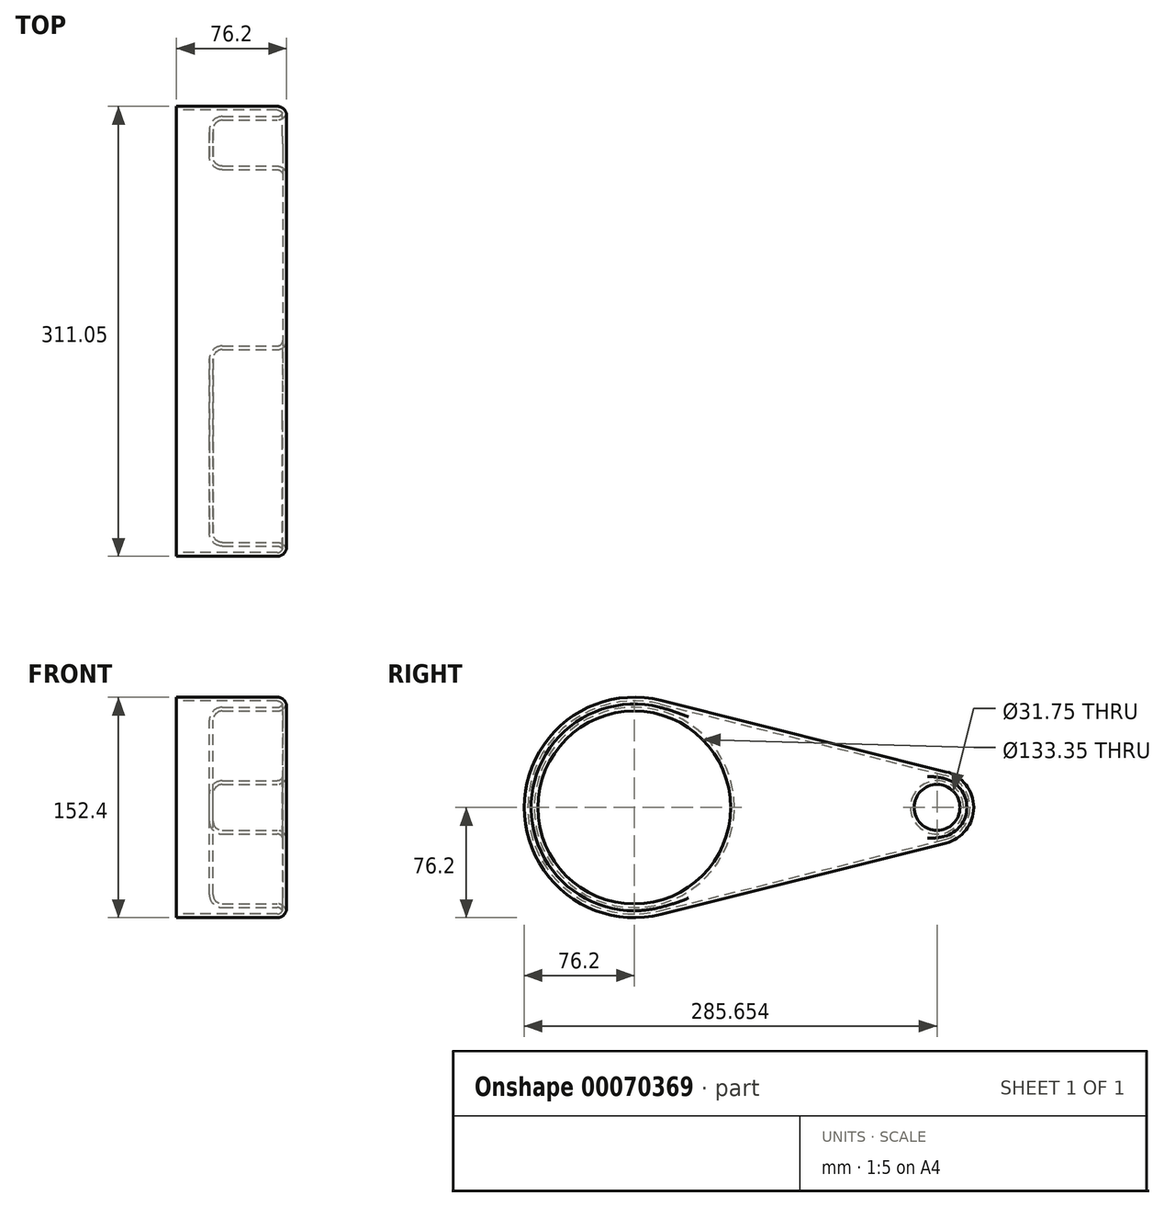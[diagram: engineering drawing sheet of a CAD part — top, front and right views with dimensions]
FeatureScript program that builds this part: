
annotation { "Feature Type Name" : "Feature", "Feature Type Description" : "" }
export const myFeature = defineFeature(function(context is Context, id is Id, definition is map)
    precondition{}
    {
        {
            var Q0;
            Q0=qCreatedBy(makeId("Right.planeOp"),FACE);
            var sketch = newSketch(context, id + "F0", { "sketchPlane" : qUnion([Q0])});
            skCircle(sketch, "E0", {"center": v(0, 0) * mm, "radius": 76.2 * mm});
            skCircle(sketch, "E1", {"center": v(209.45, 0) * mm, "radius": 25.4 * mm});
            skLineSegment(sketch, "E2", {"start": v(18.48, 73.92) * mm, "end": v(215.61, 24.64) * mm});
            skLineSegment(sketch, "E3", {"start": v(18.48, -73.92) * mm, "end": v(215.61, -24.64) * mm});
            skSolve(sketch);
        }
        {
            var Q0;
            {var subQ0=sQuery(id+"F0.wireOp",EDGE,"E0");var subQ1=makeQuery(id+"F0.imprint","INTERSECT",VERTEX,{"derivedFrom":[subQ0,sQuery(id+"F0.wireOp",EDGE,"E2")]});Q0=makeQuery(id+"F0.imprint","IMPRINT",FACE,{"disambiguationData":[TD([[makeQuery(id+"F0.imprint","IMPRINT",EDGE,{"disambiguationData":[TD([[subQ1,-1.0]])],"derivedFrom":subQ0}),1.0]])]});}
            var Q1;
            {var subQ0=sQuery(id+"F0.wireOp",EDGE,"E2");Q1=makeQuery(id+"F0.imprint","IMPRINT",FACE,{"disambiguationData":[TD([[makeQuery(id+"F0.imprint","IMPRINT",EDGE,{"derivedFrom":subQ0}),-1.0]])]});}
            var Q2;
            {var subQ0=sQuery(id+"F0.wireOp",EDGE,"E1");var subQ1=makeQuery(id+"F0.imprint","INTERSECT",VERTEX,{"derivedFrom":[subQ0,sQuery(id+"F0.wireOp",EDGE,"E2")]});Q2=makeQuery(id+"F0.imprint","IMPRINT",FACE,{"disambiguationData":[TD([[makeQuery(id+"F0.imprint","IMPRINT",EDGE,{"disambiguationData":[TD([[subQ1,-1.0]])],"derivedFrom":subQ0}),1.0]])]});}
            extrude(context, id + "F1", {"entities" : qUnion([Q0, Q1, Q2]), "depth" : 76.2 * mm});
        }
        {
            var Q0;
            Q0=makeQuery(id+"F1.opExtrude","CAP_FACE",FACE,{"disambiguationData":[OSD([sQuery(id+"F0.wireOp",EDGE,"E0"),sQuery(id+"F0.wireOp",EDGE,"E1"),sQuery(id+"F0.wireOp",EDGE,"E2"),sQuery(id+"F0.wireOp",EDGE,"E3")])],"isStart":false});
            var sketch = newSketch(context, id + "F2", { "sketchPlane" : qUnion([Q0])});
            skCircle(sketch, "E4", {"center": v(0, 0) * mm, "radius": 66.68 * mm});
            skCircle(sketch, "E5", {"center": v(209.45, 0) * mm, "radius": 15.88 * mm});
            skSolve(sketch);
        }
        {
            var Q0;
            Q0=makeQuery(id+"F2.imprint","IMPRINT",FACE,{"disambiguationData":[TD([[makeQuery(id+"F2.imprint","IMPRINT",EDGE,{"derivedFrom":sQuery(id+"F2.wireOp",EDGE,"E4")}),1.0]])]});
            var Q1;
            Q1=makeQuery(id+"F2.imprint","IMPRINT",FACE,{"disambiguationData":[TD([[makeQuery(id+"F2.imprint","IMPRINT",EDGE,{"derivedFrom":sQuery(id+"F2.wireOp",EDGE,"E5")}),1.0]])]});
            extrude(context, id + "F3", {"entities" : qUnion([Q0, Q1]), "operationType" : NewBodyOperationType.REMOVE, "oppositeDirection" : true, "depth" : 50.8 * mm});
        }
        {
            var Q0;
            Q0=makeQuery(id+"F1.opExtrude","CAP_FACE",FACE,{"disambiguationData":[OSD([sQuery(id+"F0.wireOp",EDGE,"E0"),sQuery(id+"F0.wireOp",EDGE,"E1"),sQuery(id+"F0.wireOp",EDGE,"E2"),sQuery(id+"F0.wireOp",EDGE,"E3")])],"isStart":false});
            var Q1;
            Q1=makeQuery(id+"F3.boolean.opBoolean","COPY",FACE,{"derivedFrom":makeQuery(id+"F3.opExtrude","CAP_FACE",FACE,{"disambiguationData":[OSD([sQuery(id+"F2.wireOp",EDGE,"E4")])],"isStart":false})});
            var Q2;
            Q2=makeQuery(id+"F3.boolean.opBoolean","COPY",EDGE,{"derivedFrom":makeQuery(id+"F3.opExtrude","CAP_EDGE",EDGE,{"disambiguationData":[OSD([sQuery(id+"F2.wireOp",EDGE,"E5")])],"isStart":false})});
            fillet(context, id + "F4", {"entities" : qUnion([Q0, Q1, Q2]), "radius" : 6.35 * mm, "tangentPropagation" : true, "allowEdgeOverflow" : false});
        }
        {
            var Q0;
            Q0=makeQuery(id+"F1.opExtrude","CAP_FACE",FACE,{"disambiguationData":[OSD([sQuery(id+"F0.wireOp",EDGE,"E0"),sQuery(id+"F0.wireOp",EDGE,"E1"),sQuery(id+"F0.wireOp",EDGE,"E2"),sQuery(id+"F0.wireOp",EDGE,"E3")])],"isStart":true});
            shell(context, id + "F5", {"entities" : qUnion([Q0]), "thickness" : 2.54 * mm});
        }
    });
